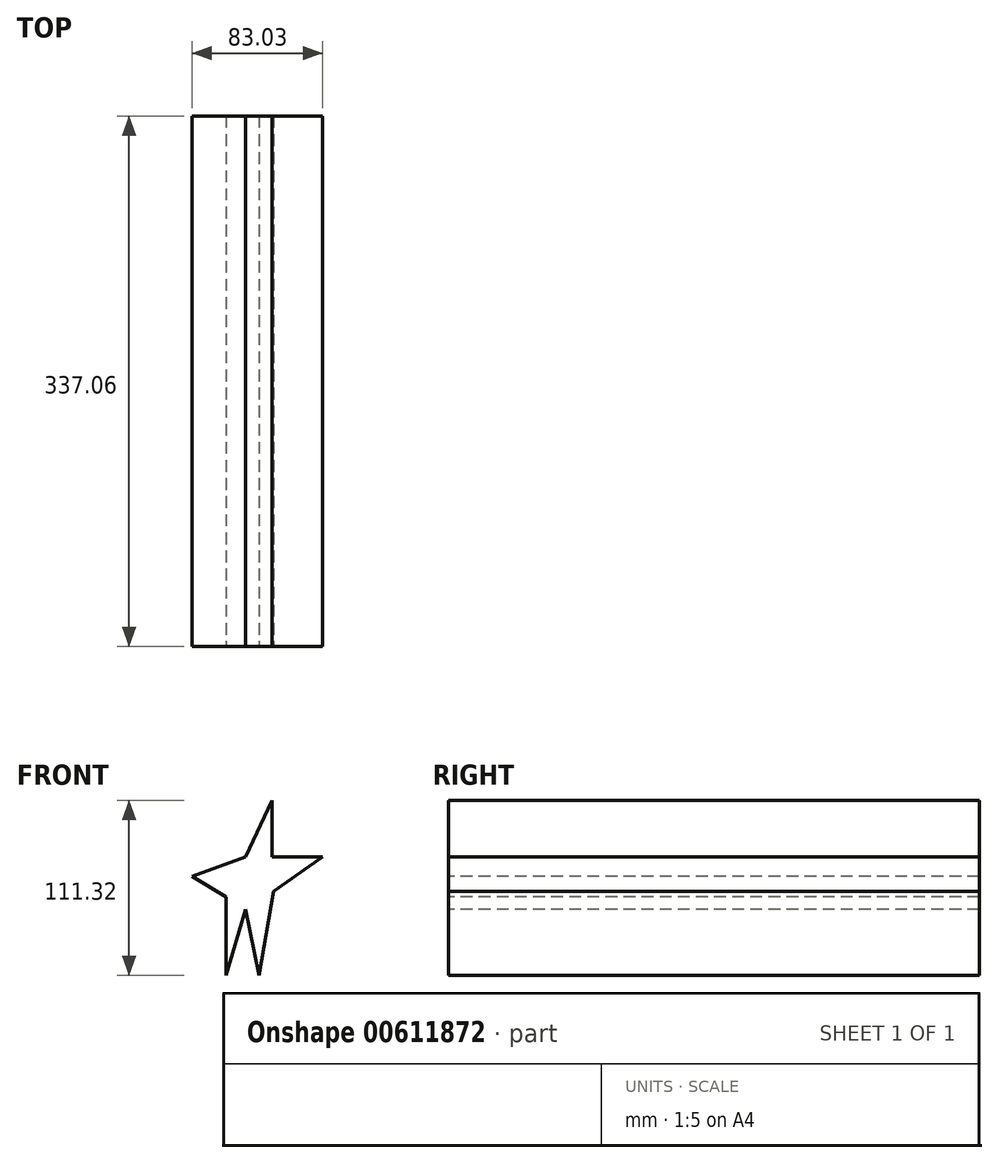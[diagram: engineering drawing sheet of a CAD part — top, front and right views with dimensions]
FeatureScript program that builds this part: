
annotation { "Feature Type Name" : "Feature", "Feature Type Description" : "" }
export const myFeature = defineFeature(function(context is Context, id is Id, definition is map)
    precondition{}
    {
        {
            var Q0;
            Q0=qCreatedBy(makeId("Front.planeOp"),FACE);
            var sketch = newSketch(context, id + "F0", { "sketchPlane" : qUnion([Q0])});
            skLineSegment(sketch, "E0", {"start": v(0, 0) * mm, "end": v(12.3, 42.06) * mm});
            skLineSegment(sketch, "E1", {"start": v(12.3, 42.06) * mm, "end": v(21.03, 0) * mm});
            skLineSegment(sketch, "E2", {"start": v(21.03, 0) * mm, "end": v(30.32, 53.27) * mm});
            skLineSegment(sketch, "E3", {"start": v(30.32, 53.27) * mm, "end": v(61.45, 75.37) * mm});
            skLineSegment(sketch, "E4", {"start": v(61.45, 75.37) * mm, "end": v(29.22, 75.37) * mm});
            skLineSegment(sketch, "E5", {"start": v(29.22, 75.37) * mm, "end": v(29.22, 111.32) * mm});
            skLineSegment(sketch, "E6", {"start": v(29.22, 111.32) * mm, "end": v(12.3, 75.37) * mm});
            skLineSegment(sketch, "E7", {"start": v(12.3, 75.37) * mm, "end": v(-21.58, 62.87) * mm});
            skLineSegment(sketch, "E8", {"start": v(-21.58, 62.87) * mm, "end": v(0, 49.97) * mm});
            skLineSegment(sketch, "E9", {"start": v(0, 49.97) * mm, "end": v(0, 0) * mm});
            skSolve(sketch);
        }
        {
            var Q0;
            Q0=makeQuery(id+"F0.imprint","IMPRINT",FACE,{"disambiguationData":[TD([[makeQuery(id+"F0.imprint","IMPRINT",EDGE,{"derivedFrom":sQuery(id+"F0.wireOp",EDGE,"E0")}),1.0]])]});
            extrude(context, id + "F1", {"entities" : qUnion([Q0]), "oppositeDirection" : true, "depth" : 337.06 * mm, "offsetDistance" : 25.4 * mm});
        }
    });
